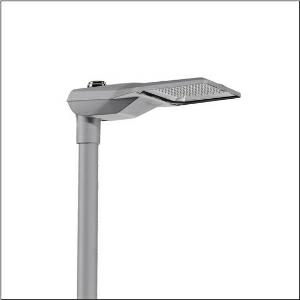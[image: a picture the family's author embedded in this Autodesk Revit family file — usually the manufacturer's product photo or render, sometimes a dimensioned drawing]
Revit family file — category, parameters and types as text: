
# Revit family: streetlight_sl_21_midi___p1_0a_5xe7a47n08mb_40bb
name_source: partatom
category: Lighting Fixtures
units: mm (PartAtom-declared; Revit-internal decimal feet)

## family parameters
Cut with Voids When Loaded = No
Host = Face
Light Source = No
Part Type = Normal
Room Calculation Point = No
Round Connector Dimension = Use Diameter
Shared = No

## types (1)
- --- (1 x LED, 20180 lm, 147 W, 4000K)
    Apparent Load = 147 VA
    CIE Flux Codes = 21 50 90 100 100
    Color Rendering = 70
    Color Temperature = 4000K
    Default Elevation = 1800 mm
    Description = Streetlight SL 21 midi, mast luminaire, primary light control with lens, of PMMA, primary optical cover: cover, of toughened safety glass, transparent, light distribution: P1.0a, light emission: direct distribution, primary light characteristic: asymmetric, installation type: side-entry, LED, 3G 2.5mm², High Power LED, rated luminous flux: 20.180lm, luminous efficacy: 137lm/W, light colour: 740, colour temperature: 4000K, control gear: NEMA (7pin), control: overheat protection, pre-setting: linear dimming characteristic, constant luminous flux control, time-dependent luminous flux control, flexible luminous flux parameterisation, mains connection: 220..240V, AC, 50/60Hz, connection cable pre-assembled, cable length: 12,5m, wiring characteristics: H05VV-F, start of lifetime: 147W, end of service life: 155W, reduction: 65W, luminaire housing, of diecast aluminium (EN AC-44300), powder-coated, Siteco® metallic grey (DB 702S), corrosivity category C5 mid according to DIN EN ISO 12944, multi-level sealing system, sealing non-destructively replaceable, inclination adjustable: 0°, 5°, 10°, 15°, length: 644mm, width: 335mm, height: 110mm, spigot size: 42mm (side-entry), mounting height: 4..8m, protection rating (complete): IP66, insulation class (complete): insulation class I (protective earthing), certification: CE, ENEC, ENEC+, VDE, impact resistance: IK10, permissible operating ambient temperature for outdoor applications: -40..+50°C, standard-compliant lighting for roads and squares, packaging unit: 1 piece

Light Distribution: P1.0a
    Height = 111 mm
    Lamp = 1 x LED
    Lamp Light Flux = 20180 lm
    Lamp Power = 147 W
    Lamp count = 1
    Length = 644 mm
    Luminous efficacy = 137 lm/W
    Manufacturer = Siteco
    ModVariant = No
    Model = 5XE7A47N08MB
    Number of Poles = 1
    OnlyDefault = Yes
    Power Factor = 1
    Product Name = Streetlight SL 21 midi | P1.0a
    Product group = mast luminaire | pylon top
    ProductGroupID = 6100
    Protection Class = Protection class I
    Protection Degree = IP 66
    RLX_Detail_Level = 1
    RLX_Emergency_Light_Flux = 0 lm
    RLX_Emergency_Type = 0
    RLX_Emergency_Type_DB = No
    RlxData = <blob elided: 37801 chars, md5=ef7ea8ea>
    Socket = socket
    Standby Power = 0 W
    System Light Flux = 20180 lm
    System Power = 147 W
    Type Comments = factory setting: luminous flux: 100 % | dim-lin: 254 | 750 mA
    Type Image = l_1294377.jpg
    URL = http://relux.com
    VarID = @adj_134444
    Voltage = 0 V
    Weight = 0.00 kg
    Width = 336 mm

## geometry (parser evidence)
native form markers: Blend x4, Sweep x10
no freeform markers — native parametric forms only
